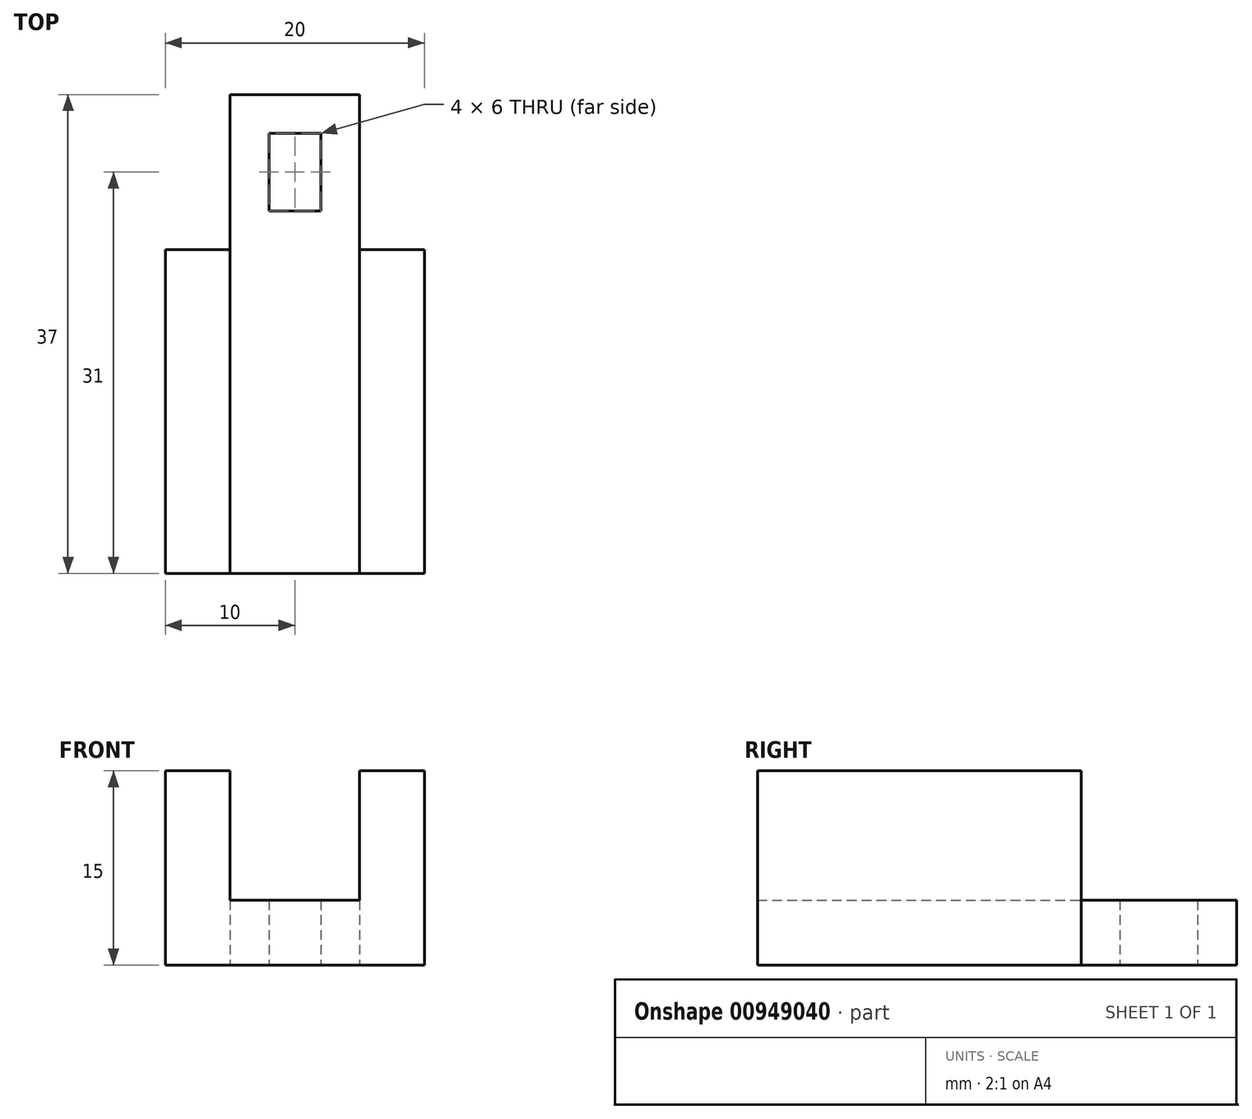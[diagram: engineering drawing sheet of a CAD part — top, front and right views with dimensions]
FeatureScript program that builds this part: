
annotation { "Feature Type Name" : "Feature", "Feature Type Description" : "" }
export const myFeature = defineFeature(function(context is Context, id is Id, definition is map)
    precondition{}
    {
        {
            var Q0;
            Q0=qCreatedBy(makeId("Front.planeOp"),FACE);
            var sketch = newSketch(context, id + "F0", { "sketchPlane" : qUnion([Q0])});
            skLineSegment(sketch, "E0", {"start": v(0, 0) * mm, "end": v(20, 0) * mm});
            skLineSegment(sketch, "E1", {"start": v(20, 0) * mm, "end": v(20, 15) * mm});
            skLineSegment(sketch, "E2", {"start": v(20, 15) * mm, "end": v(15, 15) * mm});
            skLineSegment(sketch, "E3", {"start": v(15, 15) * mm, "end": v(15, 5) * mm});
            skLineSegment(sketch, "E4", {"start": v(15, 5) * mm, "end": v(5, 5) * mm});
            skLineSegment(sketch, "E5", {"start": v(5, 5) * mm, "end": v(5, 15) * mm});
            skLineSegment(sketch, "E6", {"start": v(5, 15) * mm, "end": v(0, 15) * mm});
            skLineSegment(sketch, "E7", {"start": v(0, 15) * mm, "end": v(0, 0) * mm});
            skSolve(sketch);
        }
        {
            var Q0;
            Q0=makeQuery(id+"F0.imprint","IMPRINT",FACE,{"disambiguationData":[TD([[makeQuery(id+"F0.imprint","IMPRINT",EDGE,{"derivedFrom":sQuery(id+"F0.wireOp",EDGE,"E0")}),1.0]])]});
            extrude(context, id + "F1", {"entities" : qUnion([Q0]), "depth" : 25 * mm, "offsetDistance" : 25 * mm});
        }
        {
            var Q0;
            Q0=qCreatedBy(makeId("Top.planeOp"),FACE);
            var sketch = newSketch(context, id + "F2", { "sketchPlane" : qUnion([Q0])});
            skLineSegment(sketch, "E8", {"start": v(5, 0) * mm, "end": v(5, 12) * mm});
            skLineSegment(sketch, "E9", {"start": v(5, 12) * mm, "end": v(15, 12) * mm});
            skLineSegment(sketch, "E10", {"start": v(15, 12) * mm, "end": v(15, 0) * mm});
            skLineSegment(sketch, "E11", {"start": v(15, 0) * mm, "end": v(5, 0) * mm});
            skLineSegment(sketch, "E12.bottom", {"start": v(12, 9) * mm, "end": v(8, 9) * mm});
            skLineSegment(sketch, "E12.top", {"start": v(12, 3) * mm, "end": v(8, 3) * mm});
            skLineSegment(sketch, "E12.left", {"start": v(12, 9) * mm, "end": v(12, 3) * mm});
            skLineSegment(sketch, "E12.right", {"start": v(8, 9) * mm, "end": v(8, 3) * mm});
            skSolve(sketch);
        }
        {
            var Q0;
            Q0 = qSketchRegion(id + "F2", true);
            extrude(context, id + "F3", {"entities" : qUnion([Q0]), "operationType" : NewBodyOperationType.ADD, "depth" : 5 * mm, "offsetDistance" : 25 * mm});
        }
    });
